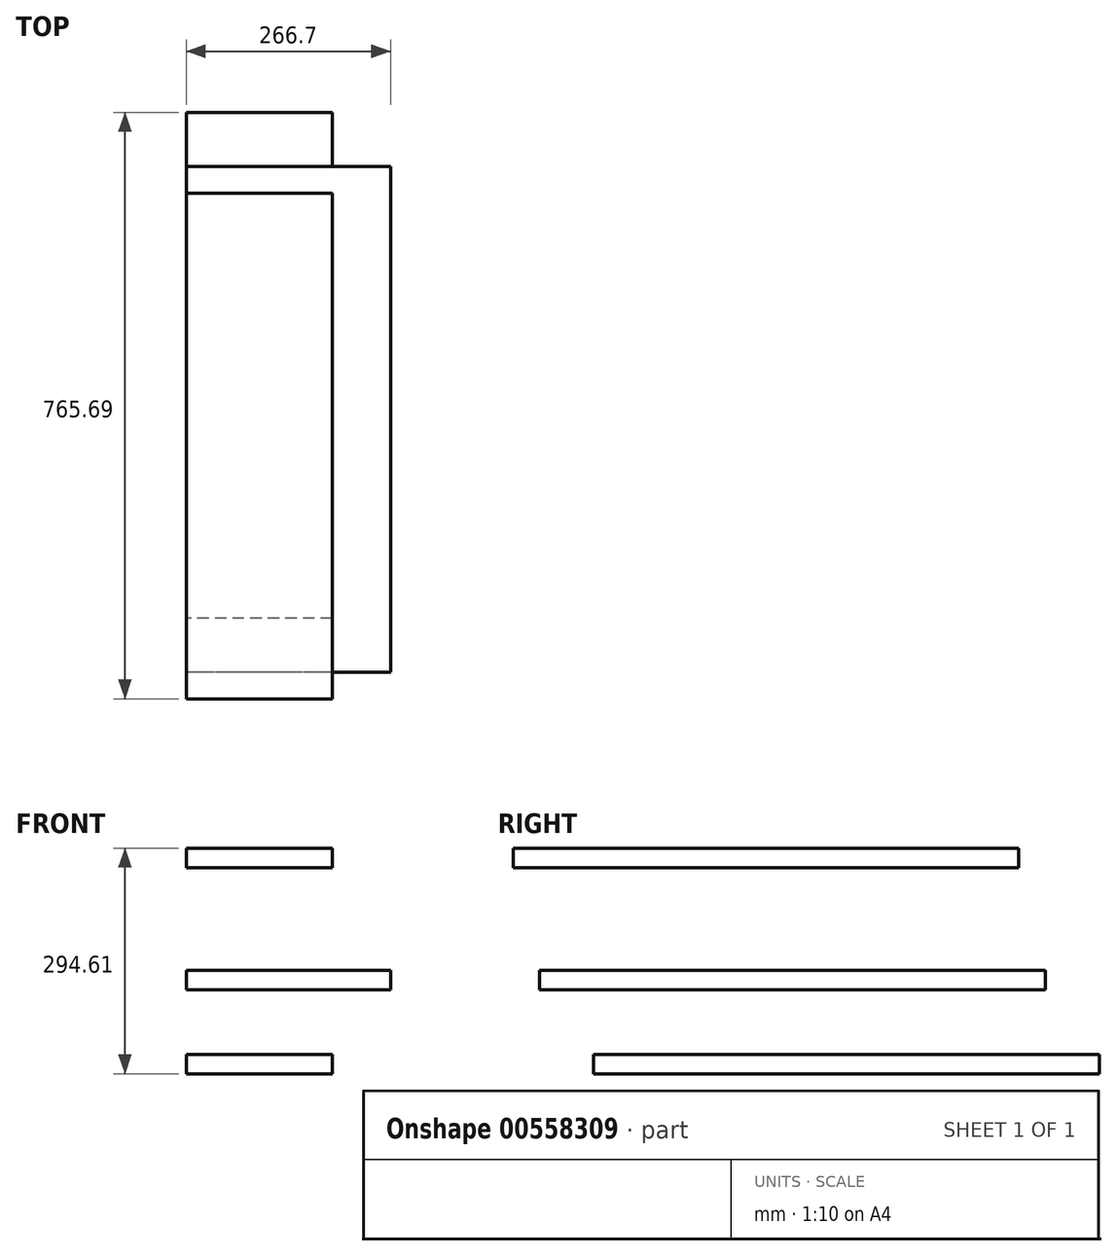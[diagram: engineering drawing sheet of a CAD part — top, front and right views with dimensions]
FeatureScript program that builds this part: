
annotation { "Feature Type Name" : "Feature", "Feature Type Description" : "" }
export const myFeature = defineFeature(function(context is Context, id is Id, definition is map)
    precondition{}
    {
        {
            var Q0;
            Q0=qCreatedBy(makeId("Right.planeOp"),FACE);
            var sketch = newSketch(context, id + "F0", { "sketchPlane" : qUnion([Q0])});
            skLineSegment(sketch, "E0.bottom", {"start": v(-224.7, 112.94) * mm, "end": v(435.7, 112.94) * mm});
            skLineSegment(sketch, "E0.top", {"start": v(-224.7, 87.54) * mm, "end": v(435.7, 87.54) * mm});
            skLineSegment(sketch, "E0.left", {"start": v(-224.7, 112.94) * mm, "end": v(-224.7, 87.54) * mm});
            skLineSegment(sketch, "E0.right", {"start": v(435.7, 112.94) * mm, "end": v(435.7, 87.54) * mm});
            skSolve(sketch);
        }
        {
            var Q0;
            Q0=qCreatedBy(makeId("Right.planeOp"),FACE);
            var sketch = newSketch(context, id + "F1", { "sketchPlane" : qUnion([Q0])});
            skLineSegment(sketch, "E1.bottom", {"start": v(-190.27, -46.75) * mm, "end": v(470.13, -46.75) * mm});
            skLineSegment(sketch, "E1.top", {"start": v(-190.27, -72.15) * mm, "end": v(470.13, -72.15) * mm});
            skLineSegment(sketch, "E1.left", {"start": v(-190.27, -46.75) * mm, "end": v(-190.27, -72.15) * mm});
            skLineSegment(sketch, "E1.right", {"start": v(470.13, -46.75) * mm, "end": v(470.13, -72.15) * mm});
            skSolve(sketch);
        }
        {
            var Q0;
            Q0=qCreatedBy(makeId("Right.planeOp"),FACE);
            var sketch = newSketch(context, id + "F2", { "sketchPlane" : qUnion([Q0])});
            skLineSegment(sketch, "E2.bottom", {"start": v(-119.4, -156.27) * mm, "end": v(541, -156.27) * mm});
            skLineSegment(sketch, "E2.top", {"start": v(-119.4, -181.67) * mm, "end": v(541, -181.67) * mm});
            skLineSegment(sketch, "E2.left", {"start": v(-119.4, -156.27) * mm, "end": v(-119.4, -181.67) * mm});
            skLineSegment(sketch, "E2.right", {"start": v(541, -156.27) * mm, "end": v(541, -181.67) * mm});
            skSolve(sketch);
        }
        {
            var Q0;
            Q0=makeQuery(id+"F0.imprint","IMPRINT",FACE,{"disambiguationData":[TD([[makeQuery(id+"F0.imprint","IMPRINT",EDGE,{"derivedFrom":sQuery(id+"F0.wireOp",EDGE,"E0.bottom")}),-1.0]])]});
            extrude(context, id + "F3", {"entities" : qUnion([Q0]), "depth" : 190.5 * mm, "offsetDistance" : 25.4 * mm});
        }
        {
            var Q0;
            Q0 = qSketchRegion(id + "F1", true);
            extrude(context, id + "F4", {"entities" : qUnion([Q0]), "depth" : 266.7 * mm, "offsetDistance" : 25.4 * mm});
        }
        {
            var Q0;
            Q0=makeQuery(id+"F2.imprint","IMPRINT",FACE,{"disambiguationData":[TD([[makeQuery(id+"F2.imprint","IMPRINT",EDGE,{"derivedFrom":sQuery(id+"F2.wireOp",EDGE,"E2.bottom")}),-1.0]])]});
            extrude(context, id + "F5", {"entities" : qUnion([Q0]), "depth" : 190.5 * mm, "offsetDistance" : 25.4 * mm});
        }
    });
